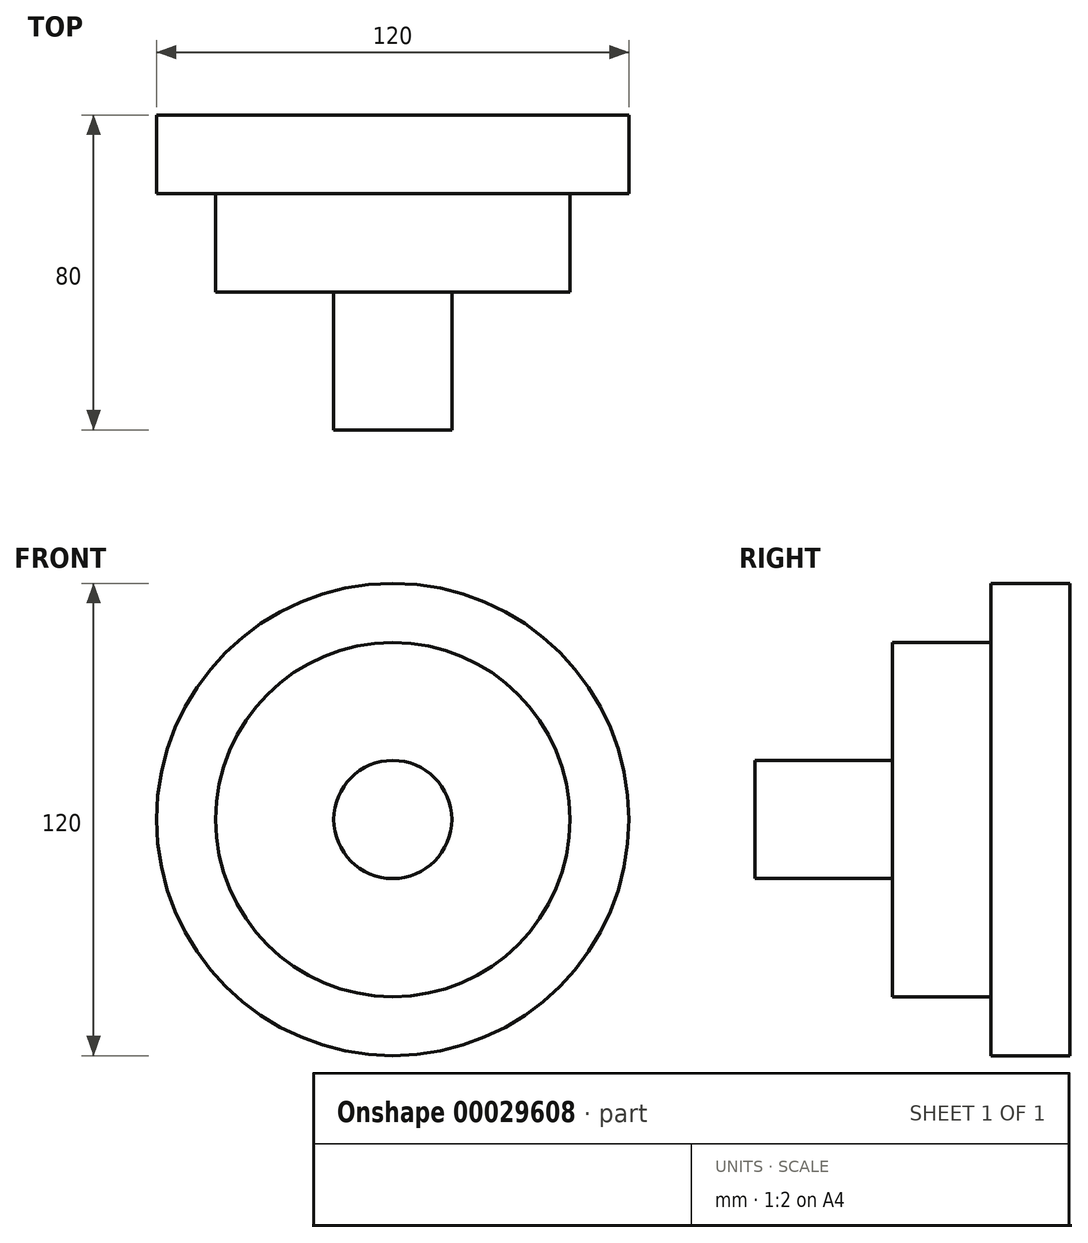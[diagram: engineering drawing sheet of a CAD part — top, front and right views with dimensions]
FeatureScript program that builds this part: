
annotation { "Feature Type Name" : "Feature", "Feature Type Description" : "" }
export const myFeature = defineFeature(function(context is Context, id is Id, definition is map)
    precondition{}
    {
        {
            var Q0;
            Q0=qCreatedBy(makeId("Front.planeOp"),FACE);
            var sketch = newSketch(context, id + "F0", { "sketchPlane" : qUnion([Q0])});
            skCircle(sketch, "E0", {"center": v(0, 0) * mm, "radius": 60 * mm});
            skCircle(sketch, "E1", {"center": v(0, 0) * mm, "radius": 45 * mm});
            skCircle(sketch, "E2", {"center": v(0, 0) * mm, "radius": 15 * mm});
            skSolve(sketch);
        }
        {
            var Q0;
            Q0=makeQuery(id+"F0.imprint","IMPRINT",FACE,{"disambiguationData":[TD([[makeQuery(id+"F0.imprint","IMPRINT",EDGE,{"derivedFrom":sQuery(id+"F0.wireOp",EDGE,"E0")}),1.0]])]});
            extrude(context, id + "F1", {"entities" : qUnion([Q0]), "depth" : 20 * mm});
        }
        {
            var Q0;
            Q0 = qSketchRegion(id + "F0", true);
            extrude(context, id + "F2", {"entities" : qUnion([Q0]), "operationType" : NewBodyOperationType.ADD, "depth" : 20 * mm});
        }
        {
            var Q0;
            Q0=makeQuery(id+"F0.imprint","IMPRINT",FACE,{"disambiguationData":[TD([[makeQuery(id+"F0.imprint","IMPRINT",EDGE,{"derivedFrom":sQuery(id+"F0.wireOp",EDGE,"E1")}),1.0]])]});
            extrude(context, id + "F3", {"entities" : qUnion([Q0]), "operationType" : NewBodyOperationType.ADD, "depth" : 45 * mm});
        }
        {
            var Q0;
            Q0=makeQuery(id+"F0.imprint","IMPRINT",FACE,{"disambiguationData":[TD([[makeQuery(id+"F0.imprint","IMPRINT",EDGE,{"derivedFrom":sQuery(id+"F0.wireOp",EDGE,"E2")}),1.0]])]});
            extrude(context, id + "F4", {"entities" : qUnion([Q0]), "operationType" : NewBodyOperationType.ADD, "depth" : 80 * mm});
        }
    });
